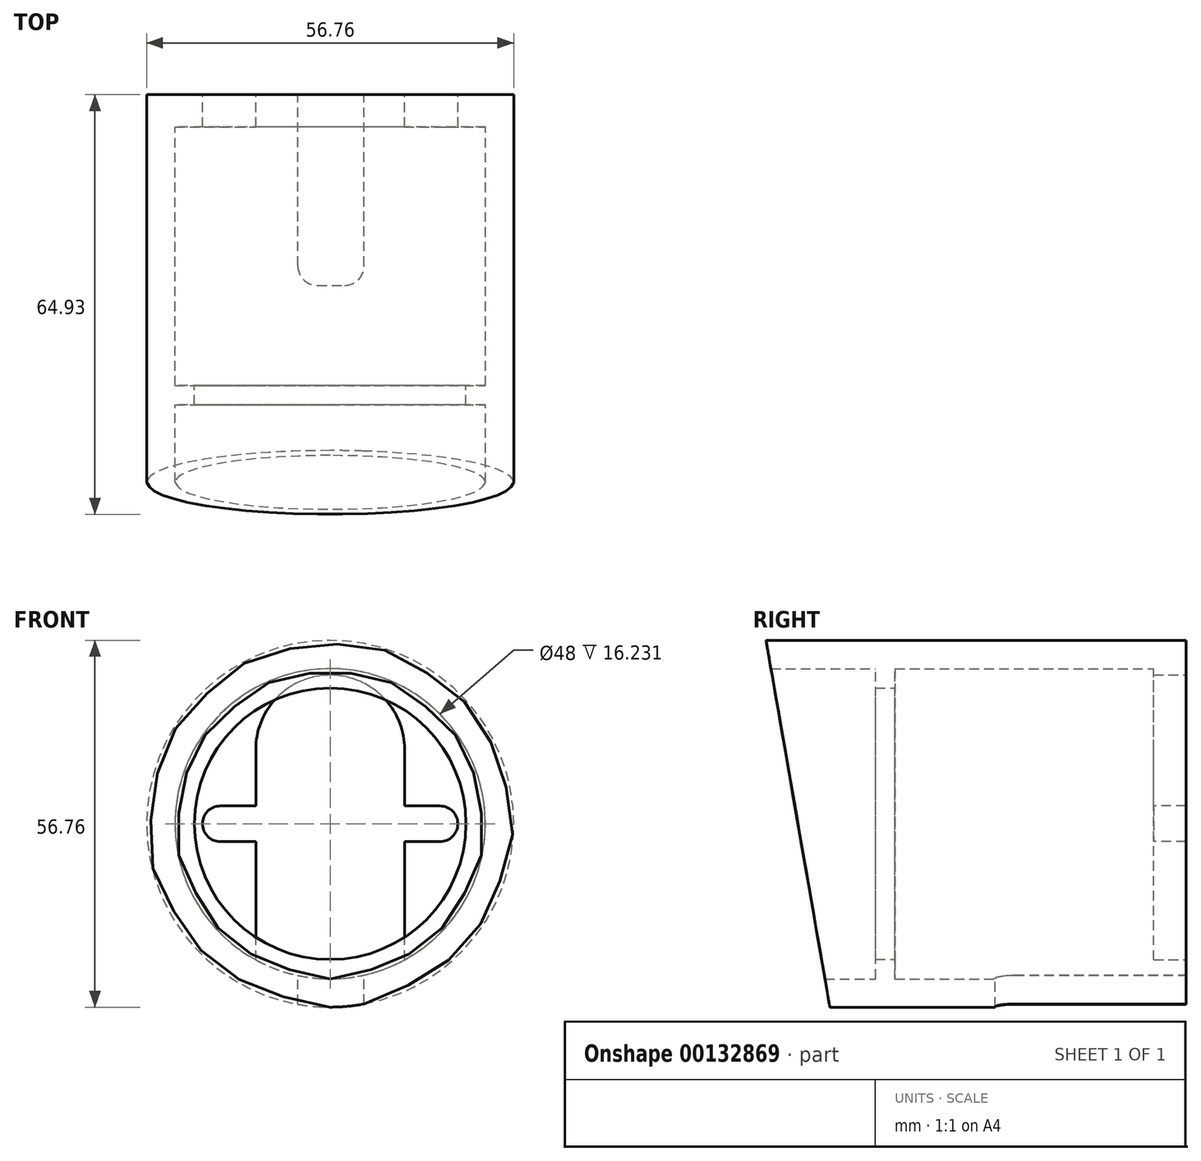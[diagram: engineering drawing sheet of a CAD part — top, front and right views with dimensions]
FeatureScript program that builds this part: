
annotation { "Feature Type Name" : "Feature", "Feature Type Description" : "" }
export const myFeature = defineFeature(function(context is Context, id is Id, definition is map)
    precondition{}
    {
        {
            var Q0;
            Q0=qCreatedBy(makeId("Front.planeOp"),FACE);
            var sketch = newSketch(context, id + "F0", { "sketchPlane" : qUnion([Q0])});
            skCircle(sketch, "E0", {"center": v(0, 0) * mm, "radius": 28.38 * mm});
            skCircle(sketch, "E1", {"center": v(0, 0) * mm, "radius": 24 * mm});
            skSolve(sketch);
        }
        {
            var Q0;
            Q0 = qSketchRegion(id + "F0", true);
            extrude(context, id + "F1", {"entities" : qUnion([Q0]), "depth" : 65 * mm});
        }
        {
            var Q0;
            Q0=qCreatedBy(makeId("Right.planeOp"),FACE);
            var sketch = newSketch(context, id + "F2", { "sketchPlane" : qUnion([Q0])});
            skLineSegment(sketch, "E2", {"start": v(-65, 28.75) * mm, "end": v(-65, -28.75) * mm});
            skLineSegment(sketch, "E3", {"start": v(-65, -28.75) * mm, "end": v(-55, -28.75) * mm});
            skLineSegment(sketch, "E4", {"start": v(-65, 28.75) * mm, "end": v(-55, -28.75) * mm});
            skSolve(sketch);
        }
        {
            var Q0;
            Q0 = qSketchRegion(id + "F2", true);
            extrude(context, id + "F3", {"entities" : qUnion([Q0]), "operationType" : NewBodyOperationType.REMOVE, "depth" : 35 * mm, "hasSecondDirection" : true, "secondDirectionOppositeDirection" : true, "secondDirectionDepth" : 35 * mm});
        }
        {
            var Q0;
            Q0=qCreatedBy(makeId("Top.planeOp"),FACE);
            var sketch = newSketch(context, id + "F4", { "sketchPlane" : qUnion([Q0])});
            skLineSegment(sketch, "E5", {"start": v(-5, 0) * mm, "end": v(-5, -26.5) * mm});
            skLineSegment(sketch, "E6", {"start": v(-2, -29.5) * mm, "end": v(2.25, -29.5) * mm});
            skLineSegment(sketch, "E7", {"start": v(5.25, -26.5) * mm, "end": v(5.25, 0) * mm});
            skLineSegment(sketch, "E8", {"start": v(5.25, 0) * mm, "end": v(-5, 0) * mm});
            skPoint(sketch, "E9.visualSharp", {"position": v(-5, -29.5) * mm});
            skArc(sketch, "E9.filletArc", {"start": v(-5, -26.5) * mm, "mid": v(-4.12, -28.62) * mm, "end": v(-2, -29.5) * mm});
            skPoint(sketch, "E10.visualSharp", {"position": v(5.25, -29.5) * mm});
            skArc(sketch, "E10.filletArc", {"start": v(2.25, -29.5) * mm, "mid": v(4.37, -28.62) * mm, "end": v(5.25, -26.5) * mm});
            skSolve(sketch);
        }
        {
            var Q0;
            Q0 = qSketchRegion(id + "F4", true);
            extrude(context, id + "F5", {"entities" : qUnion([Q0]), "operationType" : NewBodyOperationType.REMOVE, "oppositeDirection" : true, "depth" : 35 * mm});
        }
        {
            var Q0;
            Q0=qCreatedBy(makeId("Front.planeOp"),FACE);
            var sketch = newSketch(context, id + "F6", { "sketchPlane" : qUnion([Q0])});
            skArc(sketch, "E11", {"start": v(11.5, -25.53) * mm, "mid": v(0, 28) * mm, "end": v(-11.5, -25.53) * mm});
            skLineSegment(sketch, "E12", {"start": v(11.5, -25.53) * mm, "end": v(11.5, 11.5) * mm});
            skLineSegment(sketch, "E13", {"start": v(-11.5, -25.53) * mm, "end": v(-11.5, 11.5) * mm});
            skArc(sketch, "E14", {"start": v(11.5, 11.5) * mm, "mid": v(0, 23) * mm, "end": v(-11.5, 11.5) * mm});
            skSolve(sketch);
        }
        {
            var Q0;
            Q0 = qSketchRegion(id + "F6", true);
            extrude(context, id + "F7", {"entities" : qUnion([Q0]), "operationType" : NewBodyOperationType.ADD, "depth" : 5 * mm});
        }
        {
            var Q0;
            Q0=makeQuery(id+"F7.boolean.opBoolean","MERGE",FACE,{"derivedFrom":[makeQuery(id+"F1.opExtrude","CAP_FACE",FACE,{"disambiguationData":[OSD([sQuery(id+"F0.wireOp",EDGE,"E0"),sQuery(id+"F0.wireOp",EDGE,"E1")])],"isStart":true}),makeQuery(id+"F7.opExtrude","CAP_FACE",FACE,{"disambiguationData":[OSD([sQuery(id+"F6.wireOp",EDGE,"E11"),sQuery(id+"F6.wireOp",EDGE,"E12"),sQuery(id+"F6.wireOp",EDGE,"E13"),sQuery(id+"F6.wireOp",EDGE,"E14")])],"isStart":true})]});
            var sketch = newSketch(context, id + "F8", { "sketchPlane" : qUnion([Q0])});
            skArc(sketch, "E15", {"start": v(-10, -2.75) * mm, "mid": v(-7.25, 0) * mm, "end": v(-10, 2.75) * mm});
            skArc(sketch, "E16", {"start": v(10, 2.75) * mm, "mid": v(7.25, 0) * mm, "end": v(10, -2.75) * mm});
            skArc(sketch, "E17", {"start": v(-17, 2.75) * mm, "mid": v(-19.75, 0) * mm, "end": v(-17, -2.75) * mm});
            skArc(sketch, "E18", {"start": v(17, -2.75) * mm, "mid": v(19.75, 0) * mm, "end": v(17, 2.75) * mm});
            skLineSegment(sketch, "E19", {"start": v(10, 2.75) * mm, "end": v(17, 2.75) * mm});
            skLineSegment(sketch, "E20", {"start": v(10, -2.75) * mm, "end": v(17, -2.75) * mm});
            skLineSegment(sketch, "E21", {"start": v(-10, 2.75) * mm, "end": v(-17, 2.75) * mm});
            skLineSegment(sketch, "E22", {"start": v(-17, -2.75) * mm, "end": v(-10, -2.75) * mm});
            skSolve(sketch);
        }
        {
            var Q0;
            Q0 = qSketchRegion(id + "F8", true);
            extrude(context, id + "F9", {"entities" : qUnion([Q0]), "operationType" : NewBodyOperationType.REMOVE, "oppositeDirection" : true, "depth" : 25 * mm});
        }
        {
            var Q0;
            Q0=qCreatedBy(makeId("Front.planeOp"),FACE);
            cPlane(context, id + "F10", {"entities" : qUnion([Q0]), "cplaneType" : CPlaneType.OFFSET, "offset" : 45 * mm, "width" : 150 * mm, "height" : 150 * mm});
        }
        {
            var Q0;
            Q0=qCreatedBy(id+"F10.planeOp",FACE);
            var sketch = newSketch(context, id + "F11", { "sketchPlane" : qUnion([Q0])});
            skCircle(sketch, "E23", {"center": v(0, 0) * mm, "radius": 24 * mm});
            skCircle(sketch, "E24", {"center": v(0, 0) * mm, "radius": 21 * mm});
            skSolve(sketch);
        }
        {
            var Q0;
            Q0=makeQuery(id+"F11.imprint","IMPRINT",FACE,{"disambiguationData":[TD([[makeQuery(id+"F11.imprint","IMPRINT",EDGE,{"derivedFrom":sQuery(id+"F11.wireOp",EDGE,"E23")}),1.0]])]});
            extrude(context, id + "F12", {"entities" : qUnion([Q0]), "operationType" : NewBodyOperationType.ADD, "depth" : 3 * mm});
        }
    });
